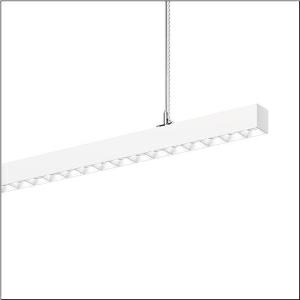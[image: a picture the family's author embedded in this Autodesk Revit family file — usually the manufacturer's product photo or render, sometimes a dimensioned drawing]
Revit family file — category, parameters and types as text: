
# Revit family: silica_r__21_51mx36da37wb_45fb
name_source: partatom
category: Lighting Fixtures
units: mm (PartAtom-declared; Revit-internal decimal feet)

## family parameters
Cut with Voids When Loaded = No
Host = Face
Light Source = No
Part Type = Normal
Room Calculation Point = No
Round Connector Dimension = Use Diameter
Shared = No

## types (1)
- --- (1 x LED, 7060 lm, 43 W, 3000K)
    Apparent Load = 43 VA
    CIE Flux Codes = 83 98 100 61 100
    Color Rendering = 80
    Color Temperature = 3000K
    Default Elevation = 1800 mm
    Description = Silica® 21, office luminaire, primary light control with darklight reflector, of PMMA, white, CAT 2 (L<= 3000cd/m²), light emission: direct/indirect distribution, primary light characteristic: symmetric, installation type: suspended mounting, LED, rated luminous flux: 7.060lm, luminous efficacy: 164lm/W, light colour: 830, colour temperature: 3000K, with terminal, 3+2-pole, max. 2.5mm², mains connection: 220..240V, AC, 50/60Hz, rated input power: 43W, luminaire housing, of aluminium, traffic white (RAL 9016), length: 1.204mm, width: 53mm, height: 53mm, protection rating (complete): IP20, insulation class (complete): insulation class I (protective earthing), certification: CE, permissible operating ambient temperature: 0..+35°C, standard: EN 50419, packaging unit: 1 piece
    Height = 53 mm
    Lamp = 1 x LED
    Lamp Light Flux = 7060 lm
    Lamp Power = 43 W
    Lamp count = 1
    Length = 1204 mm
    Luminous efficacy = 164 lm/W
    Manufacturer = Siteco
    ModVariant = No
    Model = 51MX36DA37WB
    Mounting Place = Ceiling
    Mounting Type = Pendant
    Number of Poles = 1
    OnlyDefault = Yes
    Power Factor = 1
    Product Name = Silica® 21
    Product group = office luminaire | ceiling pendant
    ProductGroupID = 902
    Protection Class = Protection class I
    Protection Degree = IP 20
    RLX_Detail_Level = 1
    RLX_Emergency_Light_Flux = 0 lm
    RLX_Emergency_Type = 0
    RLX_Emergency_Type_DB = No
    RlxData = <blob elided: 40821 chars, md5=b19d5c96>
    Socket = socket
    Standby Power = 0 W
    System Light Flux = 7060 lm
    System Power = 43 W
    Type Comments = factory setting: luminous flux: 100 % | dim-lin: 254 | 359 mA
    Type Image = l_1313634.jpg
    URL = http://relux.com
    VarID = @adj_070207
    Voltage = 0 V
    Weight = 0.00 kg
    Width = 53 mm

## geometry (parser evidence)
native form markers: Blend x4, Sweep x13
no freeform markers — native parametric forms only
